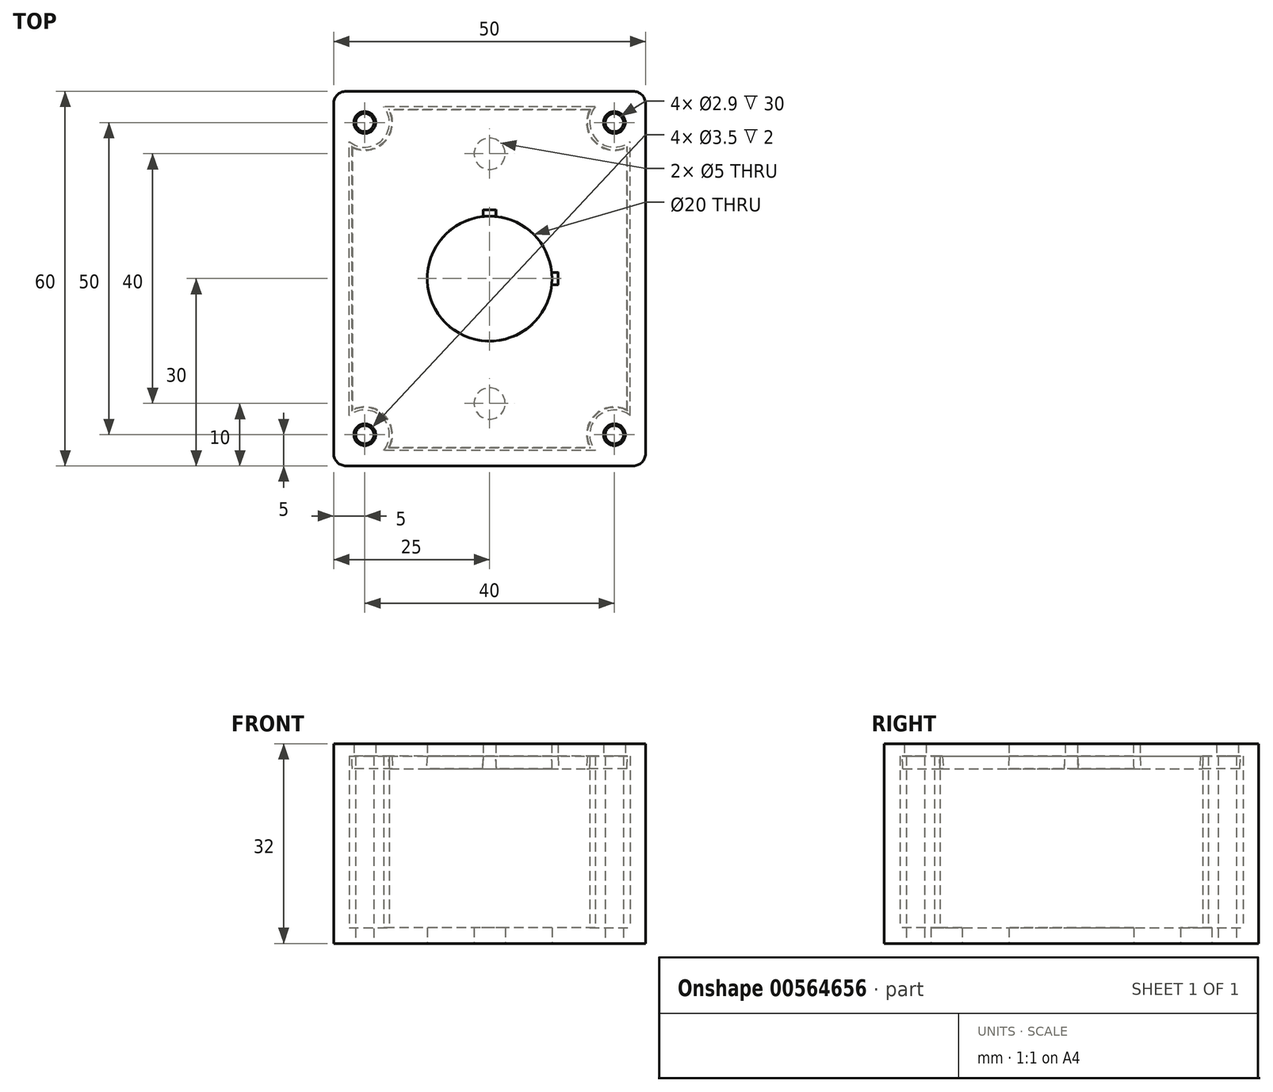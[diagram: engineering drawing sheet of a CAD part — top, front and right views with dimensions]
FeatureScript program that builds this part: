
annotation { "Feature Type Name" : "Feature", "Feature Type Description" : "" }
export const myFeature = defineFeature(function(context is Context, id is Id, definition is map)
    precondition{}
    {
        {
            var Q0;
            Q0=qCreatedBy(makeId("Top.planeOp"),FACE);
            var sketch = newSketch(context, id + "F0", { "sketchPlane" : qUnion([Q0])});
            skLineSegment(sketch, "E0.bottom", {"start": v(25, -30) * mm, "end": v(-25, -30) * mm});
            skLineSegment(sketch, "E0.top", {"start": v(25, 30) * mm, "end": v(-25, 30) * mm});
            skLineSegment(sketch, "E0.left", {"start": v(25, -30) * mm, "end": v(25, 30) * mm});
            skLineSegment(sketch, "E0.right", {"start": v(-25, -30) * mm, "end": v(-25, 30) * mm});
            skPoint(sketch, "E0.middle", {"position": v(0, 0) * mm});
            skCircle(sketch, "E1", {"center": v(-20, 25) * mm, "radius": 1.45 * mm});
            skCircle(sketch, "E2", {"center": v(20, 25) * mm, "radius": 1.45 * mm});
            skCircle(sketch, "E3", {"center": v(20, -25) * mm, "radius": 1.45 * mm});
            skCircle(sketch, "E4", {"center": v(-20, -25) * mm, "radius": 1.45 * mm});
            skCircle(sketch, "E5", {"center": v(0, 0) * mm, "radius": 10 * mm});
            skCircle(sketch, "E6", {"center": v(0, 20) * mm, "radius": 2.5 * mm});
            skCircle(sketch, "E7", {"center": v(0, -20) * mm, "radius": 2.5 * mm});
            skSolve(sketch);
        }
        {
            var Q0;
            Q0=makeQuery(id+"F0.imprint","IMPRINT",FACE,{"disambiguationData":[TD([[makeQuery(id+"F0.imprint","IMPRINT",EDGE,{"derivedFrom":sQuery(id+"F0.wireOp",EDGE,"E0.bottom")}),-1.0]])]});
            extrude(context, id + "F1", {"entities" : qUnion([Q0]), "depth" : 30 * mm, "offsetDistance" : 25 * mm});
        }
        {
            var Q0;
            Q0=makeQuery(id+"F1.opExtrude","SWEPT_FACE",FACE,{"disambiguationData":[OSD([sQuery(id+"F0.wireOp",EDGE,"E5")])]});
            var Q1;
            Q1=makeQuery(id+"F1.opExtrude","CAP_FACE",FACE,{"disambiguationData":[OSD([sQuery(id+"F0.wireOp",EDGE,"E0.bottom"),sQuery(id+"F0.wireOp",EDGE,"E0.top"),sQuery(id+"F0.wireOp",EDGE,"E0.left"),sQuery(id+"F0.wireOp",EDGE,"E0.right"),sQuery(id+"F0.wireOp",EDGE,"E1"),sQuery(id+"F0.wireOp",EDGE,"E2"),sQuery(id+"F0.wireOp",EDGE,"E3"),sQuery(id+"F0.wireOp",EDGE,"E4"),sQuery(id+"F0.wireOp",EDGE,"E5"),sQuery(id+"F0.wireOp",EDGE,"E6"),sQuery(id+"F0.wireOp",EDGE,"E7")])],"isStart":false});
            var Q2;
            Q2=makeQuery(id+"F1.opExtrude","SWEPT_FACE",FACE,{"disambiguationData":[OSD([sQuery(id+"F0.wireOp",EDGE,"E6")])]});
            var Q3;
            Q3=makeQuery(id+"F1.opExtrude","SWEPT_FACE",FACE,{"disambiguationData":[OSD([sQuery(id+"F0.wireOp",EDGE,"E7")])]});
            shell(context, id + "F2", {"entities" : qUnion([Q0, Q1, Q2, Q3]), "thickness" : 2.5 * mm});
        }
        {
            var Q0;
            Q0=makeQuery(id+"F1.opExtrude","CAP_FACE",FACE,{"disambiguationData":[OSD([sQuery(id+"F0.wireOp",EDGE,"E0.bottom"),sQuery(id+"F0.wireOp",EDGE,"E0.top"),sQuery(id+"F0.wireOp",EDGE,"E0.left"),sQuery(id+"F0.wireOp",EDGE,"E0.right"),sQuery(id+"F0.wireOp",EDGE,"E1"),sQuery(id+"F0.wireOp",EDGE,"E2"),sQuery(id+"F0.wireOp",EDGE,"E3"),sQuery(id+"F0.wireOp",EDGE,"E4"),sQuery(id+"F0.wireOp",EDGE,"E5"),sQuery(id+"F0.wireOp",EDGE,"E6"),sQuery(id+"F0.wireOp",EDGE,"E7")])],"isStart":false});
            var sketch = newSketch(context, id + "F3", { "sketchPlane" : qUnion([Q0])});
            skLineSegment(sketch, "E8.0", {"start": v(25, -30) * mm, "end": v(25, 30) * mm});
            skLineSegment(sketch, "E8.1", {"start": v(25, 30) * mm, "end": v(-25, 30) * mm});
            skLineSegment(sketch, "E8.2", {"start": v(-25, -30) * mm, "end": v(-25, 30) * mm});
            skLineSegment(sketch, "E8.3", {"start": v(25, -30) * mm, "end": v(-25, -30) * mm});
            skCircle(sketch, "E8.4", {"center": v(20, -25) * mm, "radius": 1.75 * mm});
            skCircle(sketch, "E8.5", {"center": v(20, 25) * mm, "radius": 1.75 * mm});
            skCircle(sketch, "E8.6", {"center": v(-20, 25) * mm, "radius": 1.75 * mm});
            skCircle(sketch, "E8.7", {"center": v(-20, -25) * mm, "radius": 1.75 * mm});
            skArc(sketch, "E9", {"start": v(-1, 9.95) * mm, "mid": v(-7.07, -7.07) * mm, "end": v(9.95, -1) * mm});
            skLineSegment(sketch, "E10.top", {"start": v(1, 11) * mm, "end": v(-1, 11) * mm});
            skLineSegment(sketch, "E10.left", {"start": v(1, 9.95) * mm, "end": v(1, 11) * mm});
            skLineSegment(sketch, "E10.right", {"start": v(-1, 9.95) * mm, "end": v(-1, 11) * mm});
            skPoint(sketch, "E10.middle", {"position": v(0, 10) * mm});
            skPoint(sketch, "E11.orphan", {"position": v(1, 9) * mm});
            skPoint(sketch, "E12.orphan", {"position": v(-1, 9) * mm});
            skLineSegment(sketch, "E13.bottom", {"start": v(9.95, -1) * mm, "end": v(10.95, -1) * mm});
            skLineSegment(sketch, "E13.top", {"start": v(9.95, 1) * mm, "end": v(10.95, 1) * mm});
            skLineSegment(sketch, "E13.right", {"start": v(10.95, -1) * mm, "end": v(10.95, 1) * mm});
            skPoint(sketch, "E14", {"position": v(10.95, 0) * mm});
            skPoint(sketch, "E15", {"position": v(9.95, 1) * mm});
            skPoint(sketch, "E16", {"position": v(9.95, -1) * mm});
            skPoint(sketch, "E17.orphan", {"position": v(8.95, 1) * mm});
            skArc(sketch, "E18.trimOffspring", {"start": v(9.95, 1) * mm, "mid": v(7.07, 7.07) * mm, "end": v(1, 9.95) * mm});
            skPoint(sketch, "E19.orphan", {"position": v(8.95, -1) * mm});
            skLineSegment(sketch, "E20.0", {"start": v(-22.5, -21.94) * mm, "end": v(-22.5, 21.94) * mm});
            skArc(sketch, "E20.1", {"start": v(-22.5, 21.94) * mm, "mid": v(-17.2, 22.2) * mm, "end": v(-16.94, 27.5) * mm});
            skLineSegment(sketch, "E20.2", {"start": v(16.94, 27.5) * mm, "end": v(-16.94, 27.5) * mm});
            skArc(sketch, "E20.3", {"start": v(16.94, 27.5) * mm, "mid": v(17.2, 22.2) * mm, "end": v(22.5, 21.94) * mm});
            skLineSegment(sketch, "E20.4", {"start": v(22.5, -21.94) * mm, "end": v(22.5, 21.94) * mm});
            skArc(sketch, "E20.5", {"start": v(22.5, -21.94) * mm, "mid": v(17.2, -22.2) * mm, "end": v(16.94, -27.5) * mm});
            skLineSegment(sketch, "E20.6", {"start": v(16.94, -27.5) * mm, "end": v(-16.94, -27.5) * mm});
            skArc(sketch, "E20.7", {"start": v(-16.94, -27.5) * mm, "mid": v(-17.2, -22.2) * mm, "end": v(-22.5, -21.94) * mm});
            skArc(sketch, "E21.0", {"start": v(-16.2, -27.1) * mm, "mid": v(-16.92, -21.92) * mm, "end": v(-22.1, -21.2) * mm});
            skLineSegment(sketch, "E21.1", {"start": v(16.2, -27.1) * mm, "end": v(-16.2, -27.1) * mm});
            skLineSegment(sketch, "E21.2", {"start": v(-22.1, -21.2) * mm, "end": v(-22.1, 21.2) * mm});
            skArc(sketch, "E21.3", {"start": v(22.1, -21.2) * mm, "mid": v(16.92, -21.92) * mm, "end": v(16.2, -27.1) * mm});
            skArc(sketch, "E21.4", {"start": v(-22.1, 21.2) * mm, "mid": v(-16.92, 21.92) * mm, "end": v(-16.2, 27.1) * mm});
            skLineSegment(sketch, "E21.5", {"start": v(16.2, 27.1) * mm, "end": v(-16.2, 27.1) * mm});
            skArc(sketch, "E21.6", {"start": v(16.2, 27.1) * mm, "mid": v(16.92, 21.92) * mm, "end": v(22.1, 21.2) * mm});
            skLineSegment(sketch, "E21.7", {"start": v(22.1, -21.2) * mm, "end": v(22.1, 21.2) * mm});
            skSolve(sketch);
        }
        {
            var Q0;
            Q0=makeQuery(id+"F3.imprint","IMPRINT",FACE,{"disambiguationData":[TD([[makeQuery(id+"F3.imprint","IMPRINT",EDGE,{"derivedFrom":sQuery(id+"F3.wireOp",EDGE,"E9")}),-1.0]])]});
            extrude(context, id + "F4", {"entities" : qUnion([Q0]), "oppositeDirection" : true, "depth" : 2 * mm, "offsetDistance" : 25 * mm, "hasDraft" : true, "draftAngle" : 3 * degree, "draftPullDirection" : true});
        }
        {
            var Q0;
            Q0=makeQuery(id+"F3.imprint","IMPRINT",FACE,{"disambiguationData":[TD([[makeQuery(id+"F3.imprint","IMPRINT",EDGE,{"derivedFrom":sQuery(id+"F3.wireOp",EDGE,"E20.0")}),-1.0]])]});
            var Q1;
            Q1=makeQuery(id+"F3.imprint","IMPRINT",FACE,{"disambiguationData":[TD([[makeQuery(id+"F3.imprint","IMPRINT",EDGE,{"derivedFrom":sQuery(id+"F3.wireOp",EDGE,"E9")}),-1.0]])]});
            var Q2;
            Q2=makeQuery(id+"F3.imprint","IMPRINT",FACE,{"disambiguationData":[TD([[makeQuery(id+"F3.imprint","IMPRINT",EDGE,{"derivedFrom":sQuery(id+"F3.wireOp",EDGE,"E8.0")}),1.0]])]});
            extrude(context, id + "F5", {"entities" : qUnion([Q0, Q1, Q2]), "operationType" : NewBodyOperationType.ADD, "depth" : 2 * mm, "offsetDistance" : 25 * mm});
        }
        {
            var Q0;
            Q0=makeQuery(id+"F5.opExtrude","SWEPT_EDGE",EDGE,{"disambiguationData":[OSD([sQuery(id+"F3.wireOp",EDGE,"E8.0"),sQuery(id+"F3.wireOp",EDGE,"E8.1")])]});
            var Q1;
            Q1=makeQuery(id+"F1.opExtrude","SWEPT_EDGE",EDGE,{"disambiguationData":[OSD([sQuery(id+"F0.wireOp",EDGE,"E0.top"),sQuery(id+"F0.wireOp",EDGE,"E0.left")])]});
            var Q2;
            Q2=makeQuery(id+"F5.opExtrude","SWEPT_EDGE",EDGE,{"disambiguationData":[OSD([sQuery(id+"F3.wireOp",EDGE,"E8.0"),sQuery(id+"F3.wireOp",EDGE,"E8.3")])]});
            var Q3;
            Q3=makeQuery(id+"F1.opExtrude","SWEPT_EDGE",EDGE,{"disambiguationData":[OSD([sQuery(id+"F0.wireOp",EDGE,"E0.bottom"),sQuery(id+"F0.wireOp",EDGE,"E0.left")])]});
            var Q4;
            Q4=makeQuery(id+"F5.opExtrude","SWEPT_EDGE",EDGE,{"disambiguationData":[OSD([sQuery(id+"F3.wireOp",EDGE,"E8.1"),sQuery(id+"F3.wireOp",EDGE,"E8.2")])]});
            var Q5;
            Q5=makeQuery(id+"F1.opExtrude","SWEPT_EDGE",EDGE,{"disambiguationData":[OSD([sQuery(id+"F0.wireOp",EDGE,"E0.top"),sQuery(id+"F0.wireOp",EDGE,"E0.right")])]});
            var Q6;
            Q6=makeQuery(id+"F5.opExtrude","SWEPT_EDGE",EDGE,{"disambiguationData":[OSD([sQuery(id+"F3.wireOp",EDGE,"E8.2"),sQuery(id+"F3.wireOp",EDGE,"E8.3")])]});
            var Q7;
            Q7=makeQuery(id+"F1.opExtrude","SWEPT_EDGE",EDGE,{"disambiguationData":[OSD([sQuery(id+"F0.wireOp",EDGE,"E0.bottom"),sQuery(id+"F0.wireOp",EDGE,"E0.right")])]});
            fillet(context, id + "F6", {"entities" : qUnion([Q0, Q1, Q2, Q3, Q4, Q5, Q6, Q7]), "radius" : 2 * mm, "tangentPropagation" : true, "allowEdgeOverflow" : false});
        }
    });
